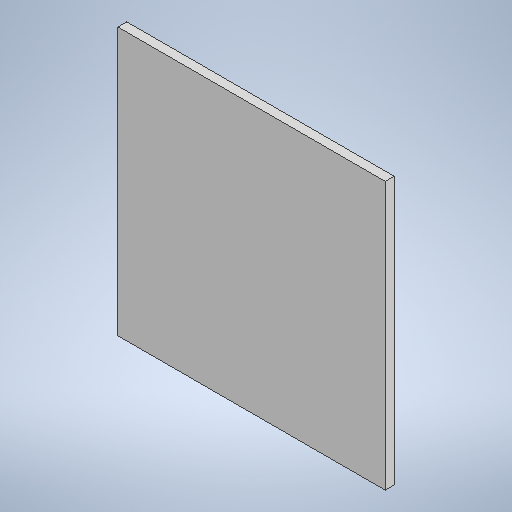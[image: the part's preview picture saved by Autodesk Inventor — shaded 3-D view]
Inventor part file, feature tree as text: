
AUTODESK INVENTOR PART (.ipt)
format: ipt  version: 2025.1 (Build 291241020, 241B)  size: 200,704 bytes
history: native  units: in
note: dims shown in document units (in); Inventor stores cm internally (conversion verified against a paired STEP export)
features: extrude x1, sketch x1
ambient origin geometry x8: Origin, YZ Plane, XZ Plane, XY Plane, X Axis, Y Axis, Z Axis, Center Point
bodies: Solid1 (feature_tree)
feature tree (2):
  extrude  "Extrusion1"  Depth=6.0in
  sketch  "Sketch1"  dims[d0=6.0in d1=6.0in d2=0.2in d3=0.0in]
